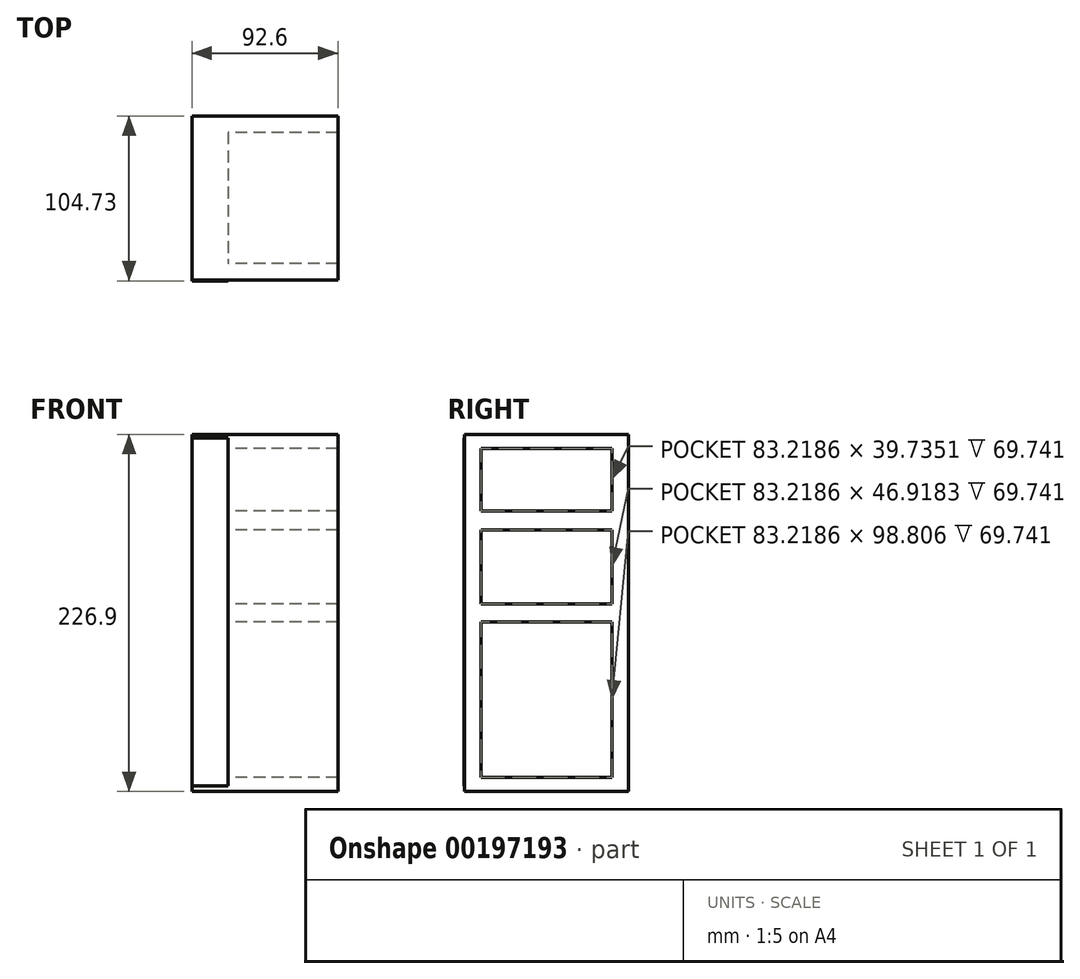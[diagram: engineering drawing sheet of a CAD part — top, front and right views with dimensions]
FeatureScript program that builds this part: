
annotation { "Feature Type Name" : "Feature", "Feature Type Description" : "" }
export const myFeature = defineFeature(function(context is Context, id is Id, definition is map)
    precondition{}
    {
        {
            var Q0;
            Q0=qCreatedBy(makeId("Right.planeOp"),FACE);
            var sketch = newSketch(context, id + "F0", { "sketchPlane" : qUnion([Q0])});
            skLineSegment(sketch, "E0.bottom", {"start": v(52.1, -113.45) * mm, "end": v(-52.1, -113.45) * mm});
            skLineSegment(sketch, "E0.top", {"start": v(52.1, 113.45) * mm, "end": v(-52.1, 113.45) * mm});
            skLineSegment(sketch, "E0.left", {"start": v(52.1, -113.45) * mm, "end": v(52.1, 113.45) * mm});
            skLineSegment(sketch, "E0.right", {"start": v(-52.1, -113.45) * mm, "end": v(-52.1, 113.45) * mm});
            skPoint(sketch, "E0.middle", {"position": v(0, 0) * mm});
            skLineSegment(sketch, "E1.bottom", {"start": v(41.6, -104.54) * mm, "end": v(-41.6, -104.54) * mm});
            skLineSegment(sketch, "E1.top", {"start": v(41.6, 104.54) * mm, "end": v(-41.6, 104.54) * mm});
            skLineSegment(sketch, "E1.left", {"start": v(41.6, -104.54) * mm, "end": v(41.6, 104.54) * mm});
            skLineSegment(sketch, "E1.right", {"start": v(-41.6, -104.54) * mm, "end": v(-41.6, 104.54) * mm});
            skLineSegment(sketch, "E2.bottom", {"start": v(41.6, -5.73) * mm, "end": v(-41.6, -5.73) * mm});
            skLineSegment(sketch, "E2.top", {"start": v(41.6, 5.73) * mm, "end": v(-41.6, 5.73) * mm});
            skLineSegment(sketch, "E2.left", {"start": v(41.6, -5.73) * mm, "end": v(41.6, 5.73) * mm});
            skLineSegment(sketch, "E2.right", {"start": v(-41.6, -5.73) * mm, "end": v(-41.6, 5.73) * mm});
            skLineSegment(sketch, "E3.bottom", {"start": v(41.6, 52.65) * mm, "end": v(-41.6, 52.65) * mm});
            skLineSegment(sketch, "E3.top", {"start": v(41.6, 64.8) * mm, "end": v(-41.6, 64.8) * mm});
            skLineSegment(sketch, "E3.left", {"start": v(41.6, 52.65) * mm, "end": v(41.6, 64.8) * mm});
            skLineSegment(sketch, "E3.right", {"start": v(-41.6, 52.65) * mm, "end": v(-41.6, 64.8) * mm});
            skPoint(sketch, "E3.middle", {"position": v(0, 58.73) * mm});
            skSolve(sketch);
        }
        {
            var Q0;
            Q0 = qSketchRegion(id + "F0", true);
            var Q1;
            Q1=makeQuery(id+"F0.imprint","IMPRINT",FACE,{"disambiguationData":[TD([[makeQuery(id+"F0.imprint","IMPRINT",EDGE,{"derivedFrom":sQuery(id+"F0.wireOp",EDGE,"E3.bottom")}),-1.0]])]});
            var Q2;
            Q2=makeQuery(id+"F0.imprint","IMPRINT",FACE,{"disambiguationData":[TD([[makeQuery(id+"F0.imprint","IMPRINT",EDGE,{"derivedFrom":sQuery(id+"F0.wireOp",EDGE,"E2.bottom")}),-1.0]])]});
            extrude(context, id + "F1", {"entities" : qUnion([Q0, Q1, Q2]), "depth" : 0.1 * yard});
        }
        {
            var Q0;
            Q0=qCreatedBy(makeId("Right.planeOp"),FACE);
            var sketch = newSketch(context, id + "F2", { "sketchPlane" : qUnion([Q0])});
            skLineSegment(sketch, "E4.bottom", {"start": v(48.12, 111.1) * mm, "end": v(-52.62, 111.1) * mm});
            skLineSegment(sketch, "E4.top", {"start": v(48.12, -109.74) * mm, "end": v(-52.62, -109.74) * mm});
            skLineSegment(sketch, "E4.left", {"start": v(48.12, 111.1) * mm, "end": v(48.12, -109.74) * mm});
            skLineSegment(sketch, "E4.right", {"start": v(-52.62, 111.1) * mm, "end": v(-52.62, -109.74) * mm});
            skSolve(sketch);
        }
        {
            var Q0;
            Q0 = qSketchRegion(id + "F2", true);
            extrude(context, id + "F3", {"entities" : qUnion([Q0]), "operationType" : NewBodyOperationType.ADD, "depth" : 0.03 * yard});
        }
    });
